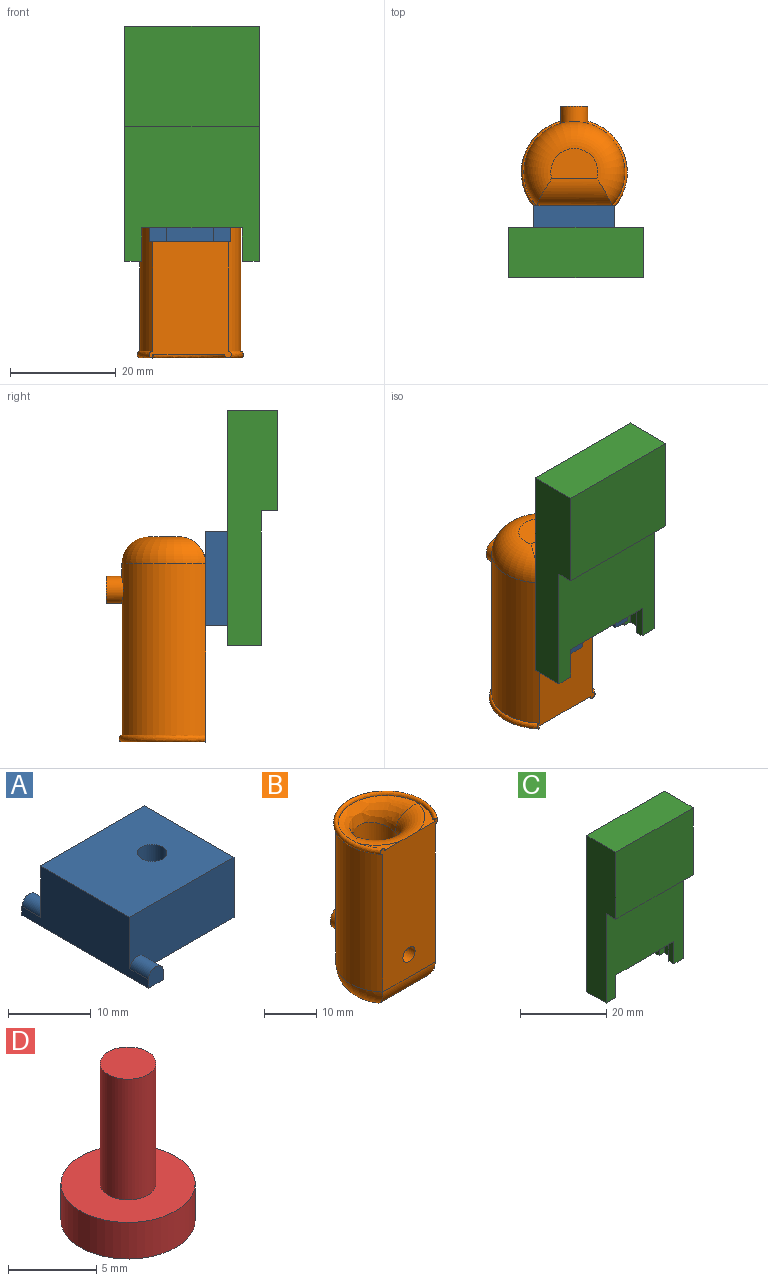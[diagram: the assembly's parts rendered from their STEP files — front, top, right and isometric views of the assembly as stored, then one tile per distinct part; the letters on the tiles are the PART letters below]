
ASSEMBLY  parts=4 mates=6
PART A: 17 faces, bbox 17.8x21.6x8.9 mm
  f0: plane 8.89x6.35mm, normal (1,0,0), area 56.5mm2, adj f3,f10,f11,f12
  f1: plane 3.18x1.27mm, normal (1,0,0), area 4mm2, adj f3,f6,f7,f15
  f2: plane 21.59x8.89mm, normal (-1,0,0), area 143.5mm2, adj f3,f5,f6,f7,f8,f9,f15,f16
  f3: plane 21.59x17.78mm, normal (0,0,-1), area 174.2mm2, adj f0,f1,f2,f4,f5,f6,f7,f8
  f4: plane 3.18x1.27mm, normal (1,0,0), area 4mm2, adj f3,f5,f8,f16
  f5: plane 2.54x2.54mm, normal (0,-1,0), area 5.8mm2, adj f2,f3,f4,f16
  f6: plane 2.54x2.54mm, normal (0,1,0), area 5.8mm2, adj f1,f2,f3,f15
  f7: plane 17.78x8.89mm, normal (0,1,0), area 152.3mm2, adj f1,f2,f3,f9,f13,f15
  f8: plane 17.78x8.89mm, normal (0,-1,0), area 152.3mm2, adj f2,f3,f4,f9,f13,f16
  f9: plane 17.78x15.24mm, normal (0,0,1), area 261mm2, adj f2,f7,f8,f13,f14
  f10: plane 12.7x6.35mm, normal (0,1,0), area 80.6mm2, adj f0,f3,f11,f13
  f11: plane 12.7x8.89mm, normal (0,0,-1), area 103mm2, adj f0,f10,f12,f13,f14
  f12: plane 12.7x6.35mm, normal (0,-1,0), area 80.6mm2, adj f0,f3,f11,f13
  f13: plane 15.24x8.89mm, normal (1,0,0), area 79mm2, adj f3,f7,f8,f9,f10,f11,f12
  f14: cylinder r=1.78mm len=3.56mm, axis (0,0,-1), area 28.4mm2, adj f9,f11
  f15: cylinder r=1.27mm len=3.18mm, axis (0,1,0), area 12.7mm2, adj f1,f2,f6,f7
  f16: cylinder r=1.27mm len=3.18mm, axis (0,1,0), area 12.7mm2, adj f2,f4,f5,f8
PART B: 17 faces, bbox 29x20x39.1 mm
  f0: plane 6.59x6.5mm, normal (0,0,1), area 8.9mm2, adj f1,f7,f8,f11
  f1: plane 33.72x15.57mm, normal (0,-1,0), area 462.8mm2, adj f0,f2,f3,f6,f7,f8,f11,f15
  f2: cylinder r=9.53mm len=32.39mm, axis (0,0,-1), area 1397.4mm2, adj f1,f5,f8,f13
  f3: plane 6.59x6.5mm, normal (0,0,1), area 8.7mm2, adj f1,f8,f11
  f4: plane 8.89x5.7mm, normal (0,0,-1), area 42mm2, adj f5,f6
  f5: torus R=4.45mm, axis (0,0,1), area 269.5mm2, adj f2,f4,f6
  f6: cylinder r=5.08mm len=14.23mm, axis (1,0,0), area 98.5mm2, adj f1,f4,f5
  f7: plane 0.73x0.72mm, normal (-0.99,-0.12,0), area 0.3mm2, adj f0,f1,f8
  f8: bspline ~28.88x18.07mm, area 115.8mm2, adj f0,f1,f2,f3,f7,f12
  f9: cylinder r=4.35mm len=21.4mm, axis (0,0,1), area 563.3mm2, adj f10,f11,f12
  f10: plane 8.69x8.69mm, normal (0,0,1), area 59.3mm2, adj f9
  f11: torus R=9.43mm, axis (0,0,1), area 126.5mm2, adj f0,f1,f3,f9,f12
  f12: bspline ~18.13x9.87mm, area 118.6mm2, adj f8,f9,f11
  f13: cylinder r=2.54mm len=5.08mm, axis (0,-1,0), area 49.6mm2, adj f2,f14
  f14: plane 5.08x5.08mm, normal (0,1,0), area 20.3mm2, adj f13
  f15: cylinder r=1.65mm len=7.87mm, axis (0,-1,0), area 81.7mm2, adj f1,f16
  f16: plane 3.3x3.3mm, normal (0,-1,0), area 8.6mm2, adj f15
PART C: 20 faces, bbox 25.4x9.5x44.5 mm
  f0: plane 6.35x3.18mm, normal (0,0,-1), area 15.1mm2, adj f1,f2,f3,f4,f8,f13,f14,f17
  f1: plane 41.91x22.23mm, normal (0,1,0), area 810.5mm2, adj f0,f4,f5,f15,f16,f17,f18,f19
  f2: plane 41.91x1.59mm, normal (1,0,0), area 66.5mm2, adj f0,f3,f14,f16
  f3: plane 41.91x1.59mm, normal (0,-1,0), area 66.5mm2, adj f0,f2,f4,f16
  f4: plane 41.91x3.18mm, normal (1,0,0), area 133.1mm2, adj f0,f1,f3,f16
  f5: plane 41.91x3.18mm, normal (-1,0,0), area 133.1mm2, adj f1,f6,f15,f16
  f6: plane 41.91x1.59mm, normal (0,-1,0), area 66.5mm2, adj f5,f7,f15,f16
  f7: plane 41.91x1.59mm, normal (-1,0,0), area 66.5mm2, adj f6,f14,f15,f16
  f8: plane 44.45x9.53mm, normal (-1,0,0), area 342.7mm2, adj f0,f9,f11,f12,f13,f14
  f9: plane 25.4x19.05mm, normal (0,-1,0), area 483.9mm2, adj f8,f10,f11,f12
  f10: plane 44.45x9.53mm, normal (1,0,0), area 342.7mm2, adj f9,f11,f12,f13,f14,f15
  f11: plane 25.4x9.53mm, normal (0,0,1), area 241.9mm2, adj f8,f9,f10,f14
  f12: plane 25.4x3.18mm, normal (0,0,-1), area 80.6mm2, adj f8,f9,f10,f13
  f13: plane 25.4x25.4mm, normal (0,-1,0), area 524.2mm2, adj f0,f8,f10,f12,f15,f17,f18,f19
  f14: plane 44.45x25.4mm, normal (0,1,0), area 330.6mm2, adj f0,f2,f7,f8,f10,f11,f15,f16
  f15: plane 6.35x3.18mm, normal (0,0,-1), area 15.1mm2, adj f1,f5,f6,f7,f10,f13,f14,f18
  f16: plane 22.23x4.76mm, normal (0,0,-1), area 100.8mm2, adj f1,f2,f3,f4,f5,f6,f7,f14
  f17: plane 6.35x1.59mm, normal (1,0,0), area 10.1mm2, adj f0,f1,f13,f19
  f18: plane 6.35x1.59mm, normal (-1,0,0), area 10.1mm2, adj f1,f13,f15,f19
  f19: plane 19.05x1.59mm, normal (0,0,-1), area 30.2mm2, adj f1,f13,f17,f18
PART D: 5 faces, bbox 7.6x7.6x10.9 mm
  f0: cylinder r=3.81mm len=7.62mm, axis (0,0,-1), area 60.8mm2, adj f1,f2
  f1: plane 7.62x7.62mm, normal (0,0,1), area 37.7mm2, adj f0,f3
  f2: plane 7.62x7.62mm, normal (0,0,-1), area 45.6mm2, adj f0
  f3: cylinder r=1.59mm len=8.38mm, axis (0,0,-1), area 83.6mm2, adj f1,f4
  f4: plane 3.18x3.18mm, normal (0,0,1), area 7.9mm2, adj f3
PLACE A rot(axis=(-0.58,0.58,0.58),120deg) t=(-2.35,3.93,-3.84)mm
PLACE B rot(axis=(0,-1,0),180deg) t=(8.44,19.15,-4.92)mm
PLACE C t=(-3.94,-0.83,-0.03)mm
PLACE D rot(axis=(-0.58,0.58,0.58),120deg) t=(8.44,7.74,-15.27)mm
MATE planar B.f1 <-> A.f9  axis (0,-1,0) through (8.45,12.82,-26.77)mm
MATE planar D.f0 <-> A.f14  axis (0,1,0) through (8.44,10.28,-15.27)mm
MATE planar A.f6 <-> C.f4  axis (-1,0,0) through (-2.35,5.08,-5.11)mm
MATE cylindrical D.f3 <-> A.f14  axis (0,-1,0) through (8.44,14.47,-15.27)mm
MATE planar A.f3 <-> C.f1  axis (0,-1,0) through (0.82,3.93,-6.38)mm
MATE cylindrical B.f15 <-> D.f3  axis (0,-1,0) through (8.44,16.76,-15.27)mm
